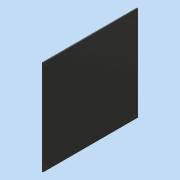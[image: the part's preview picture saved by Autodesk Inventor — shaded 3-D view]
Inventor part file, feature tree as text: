
AUTODESK INVENTOR PART (.ipt)
format: ipt  version: 2016 (Build 200138000, 138)  size: 93,696 bytes
history: native  units: mm
features: hole x4, extrude x1, sketch x1
ambient origin geometry x8: Origin, YZ Plane, XZ Plane, XY Plane, X Axis, Y Axis, Z Axis, Center Point
bodies: Solid1 (feature_tree)
feature tree (6):
  extrude  "Extrusion1"  Depth=360.0mm
  hole  "Hole1"  [1 undecoded]
  hole  "Hole2"  [1 undecoded]
  hole  "Hole3"  [1 undecoded]
  hole  "Hole4"  [1 undecoded]
  sketch  "Sketch1"  dims[d0=360.0mm d1=360.0mm d2=3.0mm d3=0.0mm d4=12.0mm d5=12.0mm d6=4.0mm d7=6.0mm d8=4.0mm d9=2.0mm d10=90.0deg d11=8.0mm d12=20.594885mm d13=12.0mm d14=12.0mm d15=4.0mm d16=6.0mm d17=4.0mm d18=2.0mm d19=90.0deg d20=8.0mm d21=20.594885mm d22=12.0mm d23=12.0mm d24=4.0mm d25=6.0mm d26=4.0mm d27=2.0mm d28=90.0deg d29=8.0mm d30=20.594885mm d31=12.0mm d32=12.0mm d33=4.0mm d34=6.0mm d35=4.0mm d36=2.0mm d37=90.0deg d38=8.0mm d39=20.594885mm]
note: 4 required parameter values undecoded (feature->parameter linkage not recoverable at this tier; creation-order binding heuristic only, values carry confidence <= 0.55)
